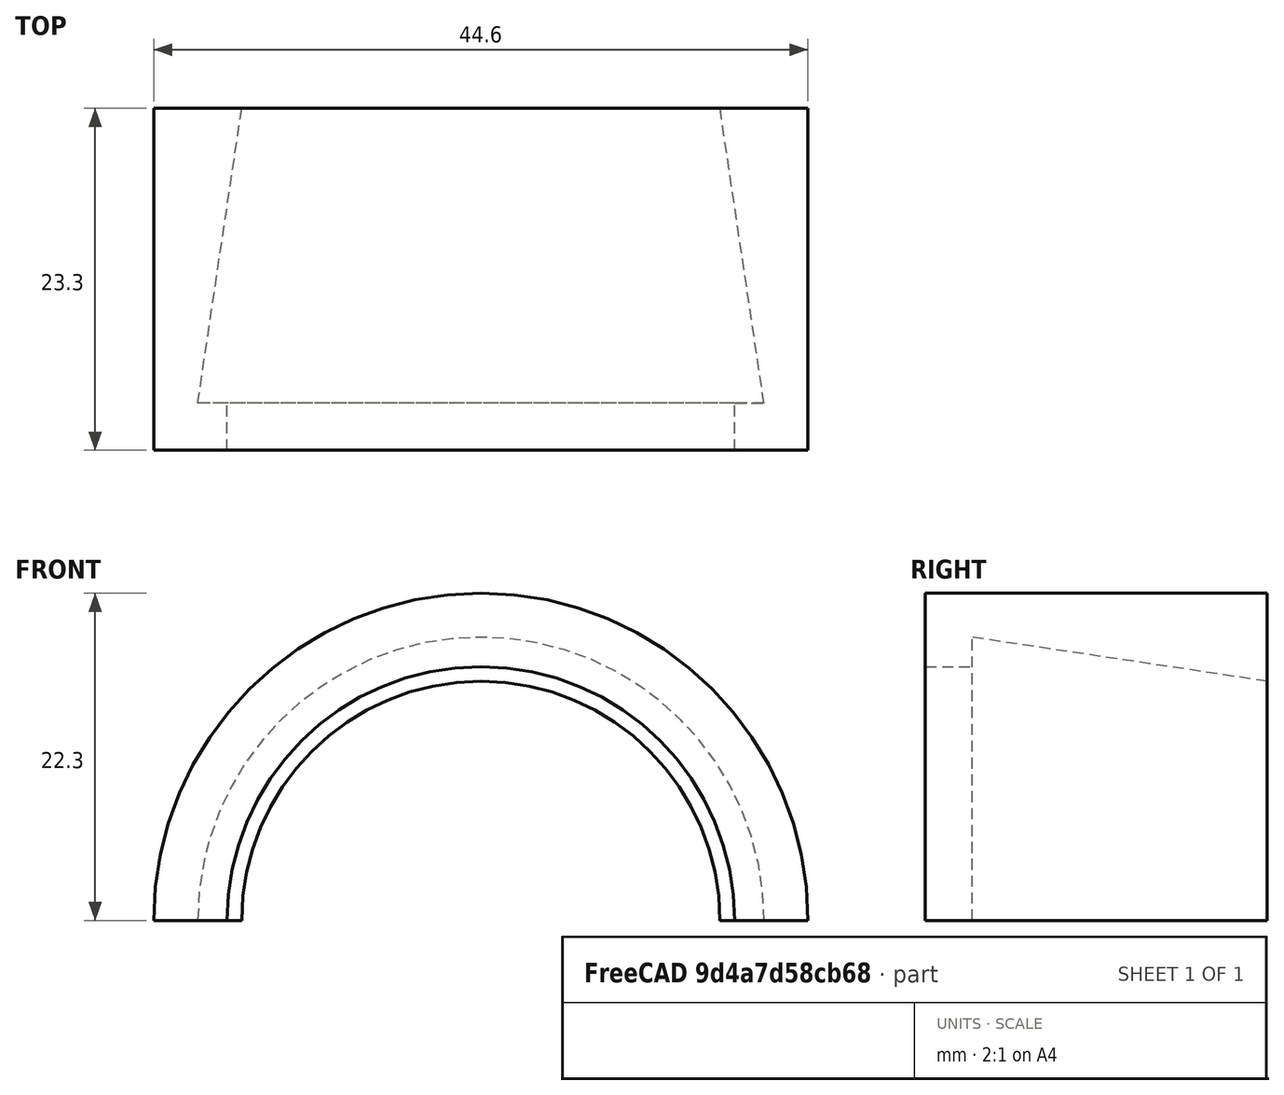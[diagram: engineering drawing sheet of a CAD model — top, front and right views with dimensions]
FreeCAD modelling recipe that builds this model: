
FCSTD DOCUMENT  (FreeCAD 0.21R33668 +26 (Git))
Label: eyepiece
License: Creative Commons Attribution 4.0
LicenseURL: https://creativecommons.org/licenses/by/4.0/
objects: Sketcher::SketchObject×1, PartDesign::Revolution×1, PartDesign::Body×1
note: 4 computed .brp shape members not serialized (recipe doc carries the construction recipe); baked Part::Feature solids carry a one-line shape summary decoded from their .brp

FEATURE [Sketcher::SketchObject] Sketch
  FullyConstrained = true
  MapMode = 5
  Support = -> [XY_Plane]
  expr: Constraints[16] = 34.6 / 2
  sketch-geometry (6):
    g0: LineSegment StartX=17.3 StartY=0 StartZ=0 EndX=17.3 EndY=3.2 EndZ=0
    g1: LineSegment StartX=17.3 StartY=3.2 StartZ=0 EndX=19.3 EndY=3.2 EndZ=0
    g2: LineSegment StartX=19.3 StartY=3.2 StartZ=0 EndX=16.3 EndY=23.3 EndZ=0
    g3: LineSegment StartX=16.3 StartY=23.3 StartZ=0 EndX=22.3 EndY=23.3 EndZ=0
    g4: LineSegment StartX=22.3 StartY=23.3 StartZ=0 EndX=22.3 EndY=0 EndZ=0
    g5: LineSegment StartX=22.3 StartY=0 StartZ=0 EndX=17.3 EndY=0 EndZ=0
  constraints (18):
    c: PointOnObject(g0,g-1)
    c: Coincident(g0,g1)
    c: Coincident(g1,g2)
    c: Coincident(g2,g3)
    c: Coincident(g3,g4)
    c: PointOnObject(g4,g-1)
    c: Vertical(g4)
    c: Coincident(g4,g5)
    c: Coincident(g5,g0)
    c: Horizontal(g1)
    c: Horizontal(g3)
    c: Distance(g1,g5) = 3.2
    c: DistanceY(g4,g4) = 23.3
    c: DistanceX(g3,g3) = 6
    c: DistanceX(g5,g5) = 5
    c: Distance(g1,g4) = 3
    c: Distance(g-1,g0) = 17.3
    c: DistanceX(g1,g1) = 2
FEATURE [PartDesign::Revolution] Revolution
  Angle = 180
  Axis = (0,1,0)
  Base = (0,0,0)
  Profile = -> Sketch
  ReferenceAxis = -> Sketch [V_Axis]
  Reversed = true
FEATURE [PartDesign::Body] Body
  Group = -> [Sketch,Revolution]
  Origin = -> Origin
  Tip = -> Revolution
